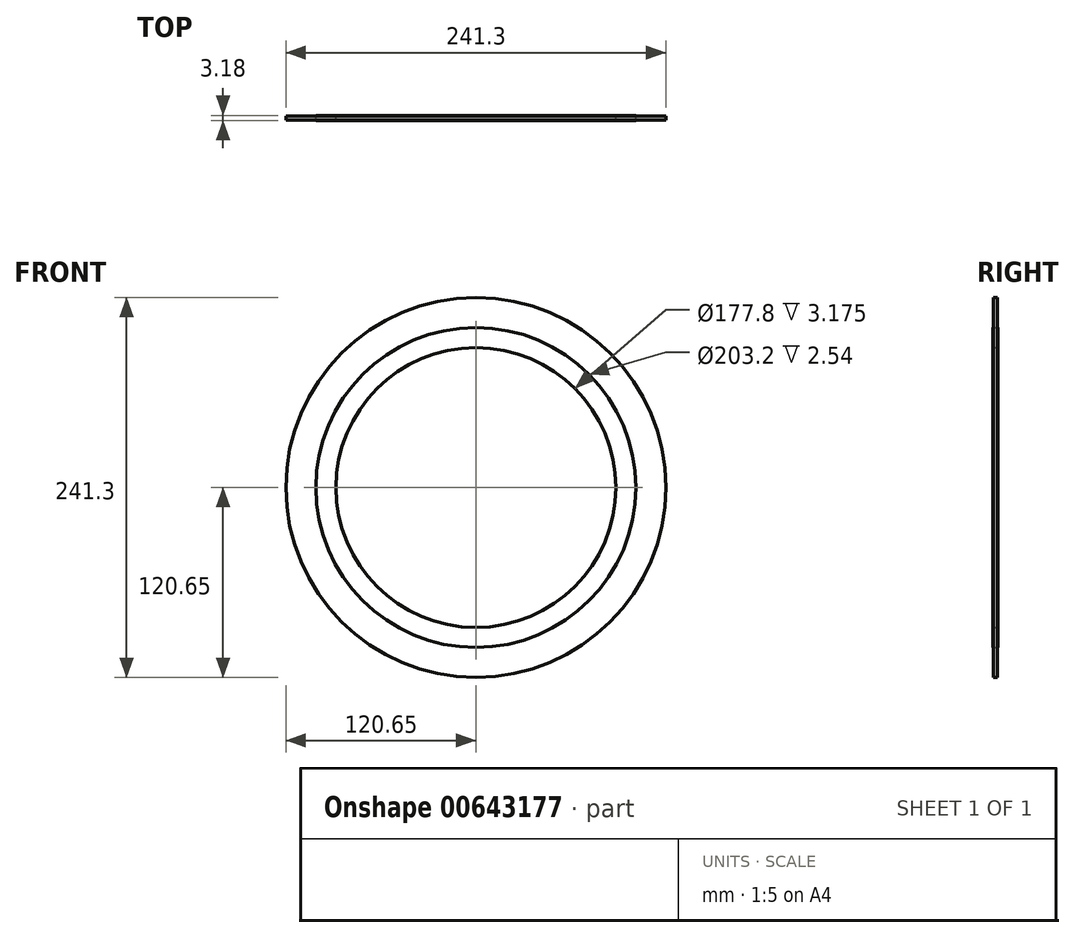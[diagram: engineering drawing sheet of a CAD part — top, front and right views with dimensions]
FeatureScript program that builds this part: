
annotation { "Feature Type Name" : "Feature", "Feature Type Description" : "" }
export const myFeature = defineFeature(function(context is Context, id is Id, definition is map)
    precondition{}
    {
        {
            var Q0;
            Q0=qCreatedBy(makeId("Front.planeOp"),FACE);
            var sketch = newSketch(context, id + "F0", { "sketchPlane" : qUnion([Q0])});
            skCircle(sketch, "E0", {"center": v(0, 0) * mm, "radius": 120.65 * mm});
            skCircle(sketch, "E1", {"center": v(0, 0) * mm, "radius": 101.6 * mm});
            skSolve(sketch);
        }
        {
            var Q0;
            Q0=makeQuery(id+"F0.imprint","IMPRINT",FACE,{"disambiguationData":[TD([[makeQuery(id+"F0.imprint","IMPRINT",EDGE,{"derivedFrom":sQuery(id+"F0.wireOp",EDGE,"E0")}),1.0]])]});
            extrude(context, id + "F1", {"entities" : qUnion([Q0]), "depth" : 2.54 * mm, "offsetDistance" : 25.4 * mm, "symmetric" : true});
        }
        {
            var Q0;
            Q0=qCreatedBy(makeId("Front.planeOp"),FACE);
            var sketch = newSketch(context, id + "F2", { "sketchPlane" : qUnion([Q0])});
            skCircle(sketch, "E2", {"center": v(0, 0) * mm, "radius": 88.9 * mm});
            skCircle(sketch, "E3", {"center": v(0, 0) * mm, "radius": 101.6 * mm});
            skSolve(sketch);
        }
        {
            var Q0;
            Q0 = qSketchRegion(id + "F2", true);
            extrude(context, id + "F3", {"entities" : qUnion([Q0]), "depth" : 3.17 * mm, "offsetDistance" : 25.4 * mm, "symmetric" : true});
        }
    });
